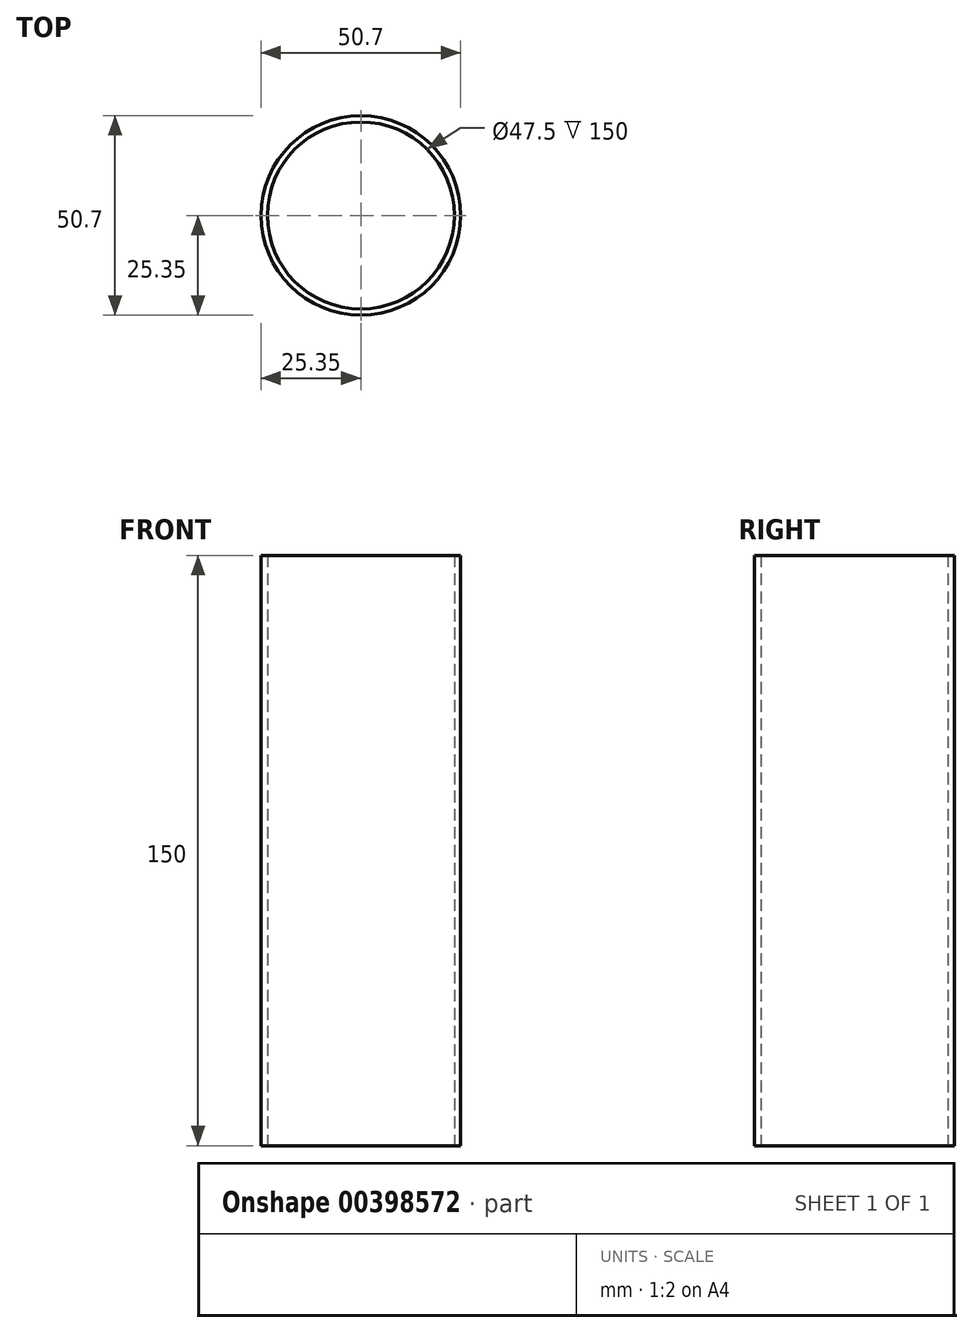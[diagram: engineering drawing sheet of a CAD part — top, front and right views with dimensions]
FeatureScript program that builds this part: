
annotation { "Feature Type Name" : "Feature", "Feature Type Description" : "" }
export const myFeature = defineFeature(function(context is Context, id is Id, definition is map)
    precondition{}
    {
        {
            var Q0;
            Q0=qCreatedBy(makeId("Top.planeOp"),FACE);
            var sketch = newSketch(context, id + "F0", { "sketchPlane" : qUnion([Q0])});
            skCircle(sketch, "E0", {"center": v(0, 0) * mm, "radius": 25.35 * mm});
            skCircle(sketch, "E1", {"center": v(0, 0) * mm, "radius": 23.75 * mm});
            skSolve(sketch);
        }
        {
            var Q0;
            Q0=makeQuery(id+"F0.imprint","IMPRINT",FACE,{"disambiguationData":[TD([[makeQuery(id+"F0.imprint","IMPRINT",EDGE,{"derivedFrom":sQuery(id+"F0.wireOp",EDGE,"E0")}),1.0]])]});
            extrude(context, id + "F1", {"entities" : qUnion([Q0]), "depth" : 150 * mm});
        }
    });
